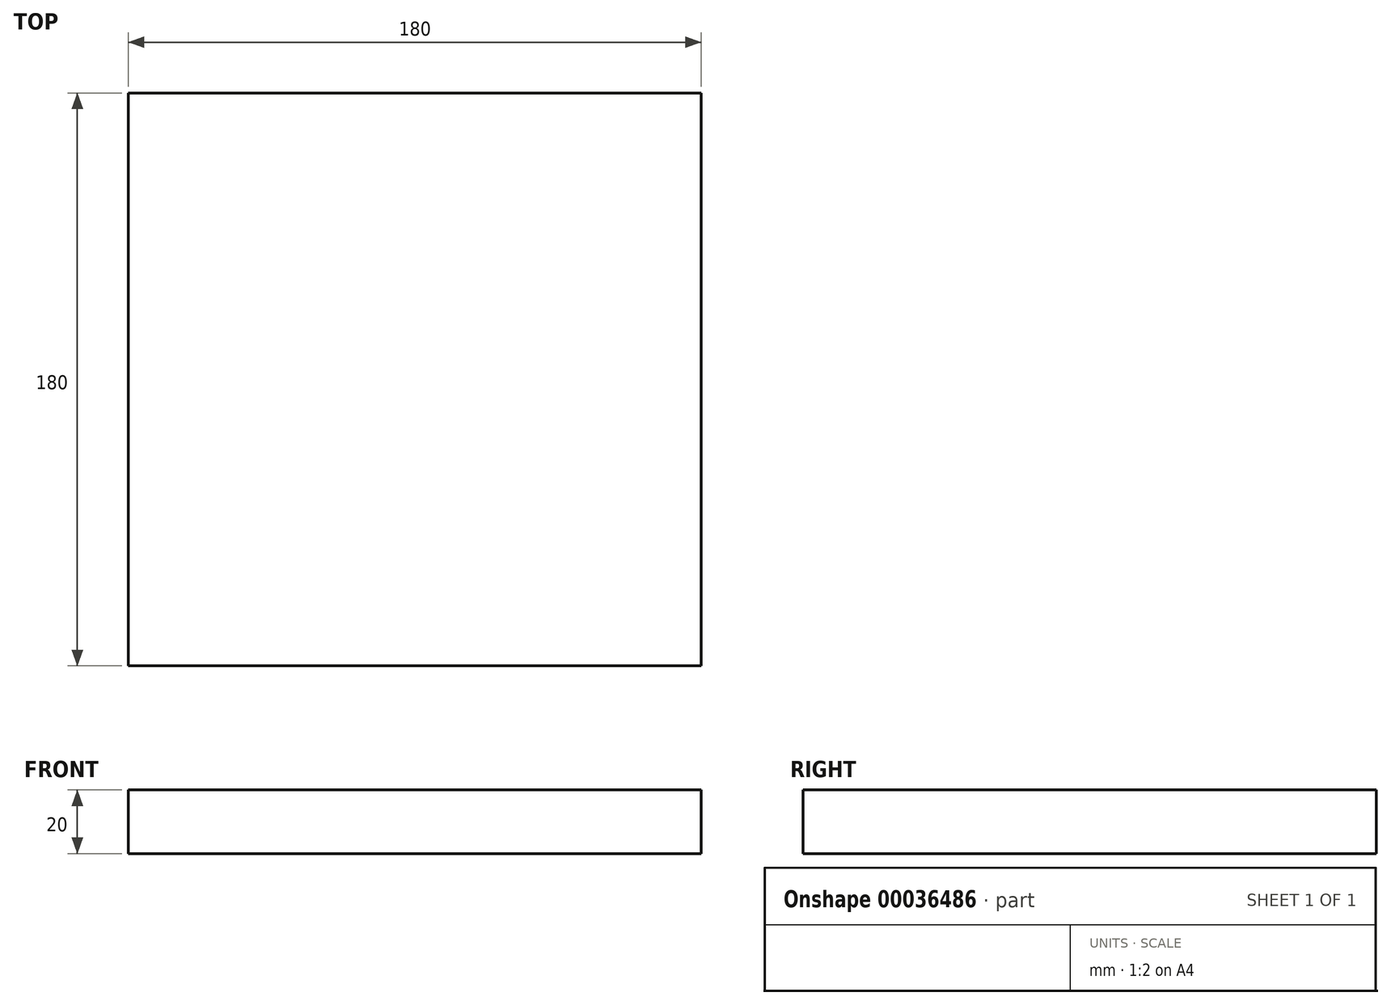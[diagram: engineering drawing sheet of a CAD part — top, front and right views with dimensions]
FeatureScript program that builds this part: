
annotation { "Feature Type Name" : "Feature", "Feature Type Description" : "" }
export const myFeature = defineFeature(function(context is Context, id is Id, definition is map)
    precondition{}
    {
        {
            var Q0;
            Q0=qCreatedBy(makeId("Top.planeOp"),FACE);
            var sketch = newSketch(context, id + "F0", { "sketchPlane" : qUnion([Q0])});
            skLineSegment(sketch, "E0.bottom", {"start": v(-84, 86.12) * mm, "end": v(84, 86.12) * mm});
            skLineSegment(sketch, "E0.top", {"start": v(-84, -81.88) * mm, "end": v(84, -81.88) * mm});
            skLineSegment(sketch, "E0.left", {"start": v(-84, 86.12) * mm, "end": v(-84, -81.88) * mm});
            skLineSegment(sketch, "E0.right", {"start": v(84, 86.12) * mm, "end": v(84, -81.88) * mm});
            skSolve(sketch);
        }
        {
            var Q0;
            Q0=makeQuery(id+"F0.imprint","IMPRINT",FACE,{"disambiguationData":[TD([[makeQuery(id+"F0.imprint","IMPRINT",EDGE,{"derivedFrom":sQuery(id+"F0.wireOp",EDGE,"E0.bottom")}),-1.0]])]});
            extrude(context, id + "F1", {"entities" : qUnion([Q0]), "depth" : 20 * mm});
        }
        {
            var Q0;
            Q0=makeQuery(id+"F1.opExtrude","SWEPT_FACE",FACE,{"disambiguationData":[OSD([sQuery(id+"F0.wireOp",EDGE,"E0.bottom")])]});
            extrude(context, id + "F2", {"entities" : qUnion([Q0]), "operationType" : NewBodyOperationType.ADD, "depth" : 12 * mm});
        }
        {
            var Q0;
            {var subQ0=sQuery(id+"F0.wireOp",EDGE,"E0.left");Q0=makeQuery(id+"F2.boolean.opBoolean","MERGE",FACE,{"derivedFrom":[makeQuery(id+"F1.opExtrude","SWEPT_FACE",FACE,{"disambiguationData":[OSD([subQ0])]}),makeQuery(id+"F2.opExtrude","SWEPT_FACE",FACE,{"disambiguationData":[OSD([sQuery(id+"F0.wireOp",EDGE,"E0.bottom"),subQ0])]})]});}
            extrude(context, id + "F3", {"entities" : qUnion([Q0]), "operationType" : NewBodyOperationType.ADD, "depth" : 12 * mm});
        }
    });
